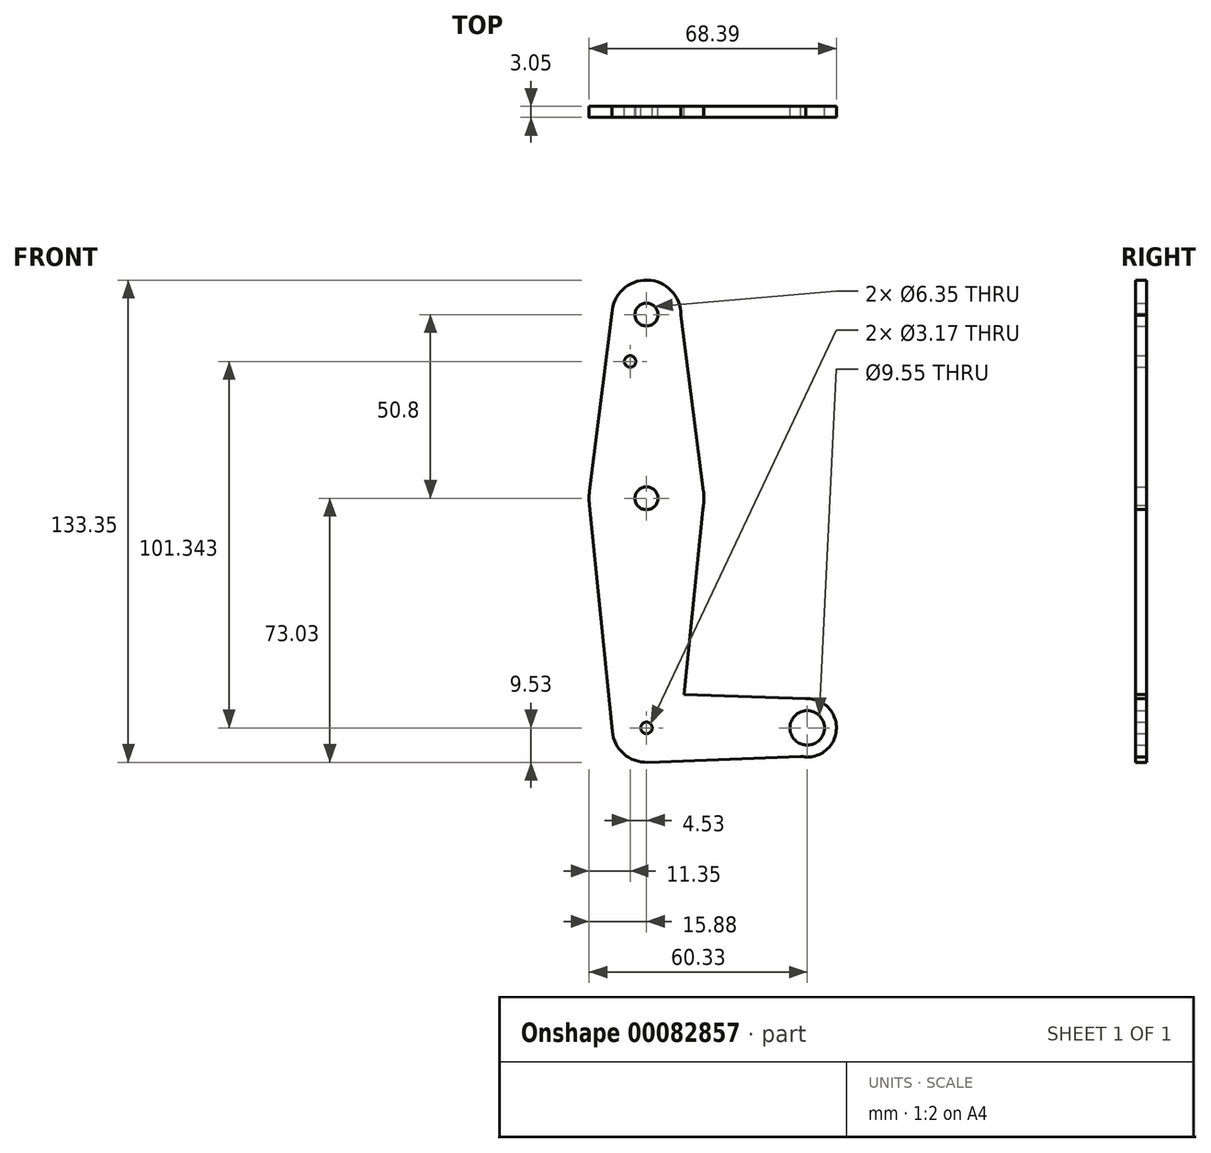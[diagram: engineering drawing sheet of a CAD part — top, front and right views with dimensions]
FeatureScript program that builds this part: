
annotation { "Feature Type Name" : "Feature", "Feature Type Description" : "" }
export const myFeature = defineFeature(function(context is Context, id is Id, definition is map)
    precondition{}
    {
        {
            var Q0;
            Q0=qCreatedBy(makeId("Front.planeOp"),FACE);
            var sketch = newSketch(context, id + "F0", { "sketchPlane" : qUnion([Q0])});
            skLineSegment(sketch, "E0", {"start": v(0, 50.8) * mm, "end": v(0, -63.5) * mm, "construction": true});
            skLineSegment(sketch, "E1", {"start": v(0, -63.5) * mm, "end": v(44.45, -63.5) * mm});
            skCircle(sketch, "E2", {"center": v(0, 50.8) * mm, "radius": 9.53 * mm});
            skCircle(sketch, "E3", {"center": v(0, 0) * mm, "radius": 15.88 * mm});
            skCircle(sketch, "E4", {"center": v(0, -63.5) * mm, "radius": 9.53 * mm});
            skCircle(sketch, "E5", {"center": v(44.45, -63.5) * mm, "radius": 8.06 * mm});
            skLineSegment(sketch, "E6", {"start": v(9.52, 50.68) * mm, "end": v(15.75, 2.01) * mm});
            skLineSegment(sketch, "E7", {"start": v(15.88, 0) * mm, "end": v(9.53, -63.5) * mm});
            skLineSegment(sketch, "E8", {"start": v(-9.52, 51.15) * mm, "end": v(-15.75, 2) * mm});
            skLineSegment(sketch, "E9", {"start": v(-15.76, -1.92) * mm, "end": v(-9.48, -64.45) * mm});
            skLineSegment(sketch, "E10", {"start": v(45.4, -55.5) * mm, "end": v(0.32, -53.98) * mm});
            skLineSegment(sketch, "E11", {"start": v(46.87, -71.2) * mm, "end": v(0, -73.03) * mm});
            skCircle(sketch, "E12", {"center": v(-4.53, 37.84) * mm, "radius": 1.59 * mm});
            skCircle(sketch, "E13", {"center": v(0, 0) * mm, "radius": 1.59 * mm});
            skCircle(sketch, "E14", {"center": v(0, -63.5) * mm, "radius": 1.59 * mm});
            skCircle(sketch, "E15", {"center": v(44.45, -63.5) * mm, "radius": 4.77 * mm});
            skCircle(sketch, "E16", {"center": v(0, 50.8) * mm, "radius": 3.18 * mm});
            skCircle(sketch, "E17", {"center": v(0, 0) * mm, "radius": 3.18 * mm});
            skSolve(sketch);
        }
        {
            var Q0;
            Q0 = qSketchRegion(id + "F0", true);
            extrude(context, id + "F1", {"entities" : qUnion([Q0]), "depth" : 3.05 * mm});
        }
    });
